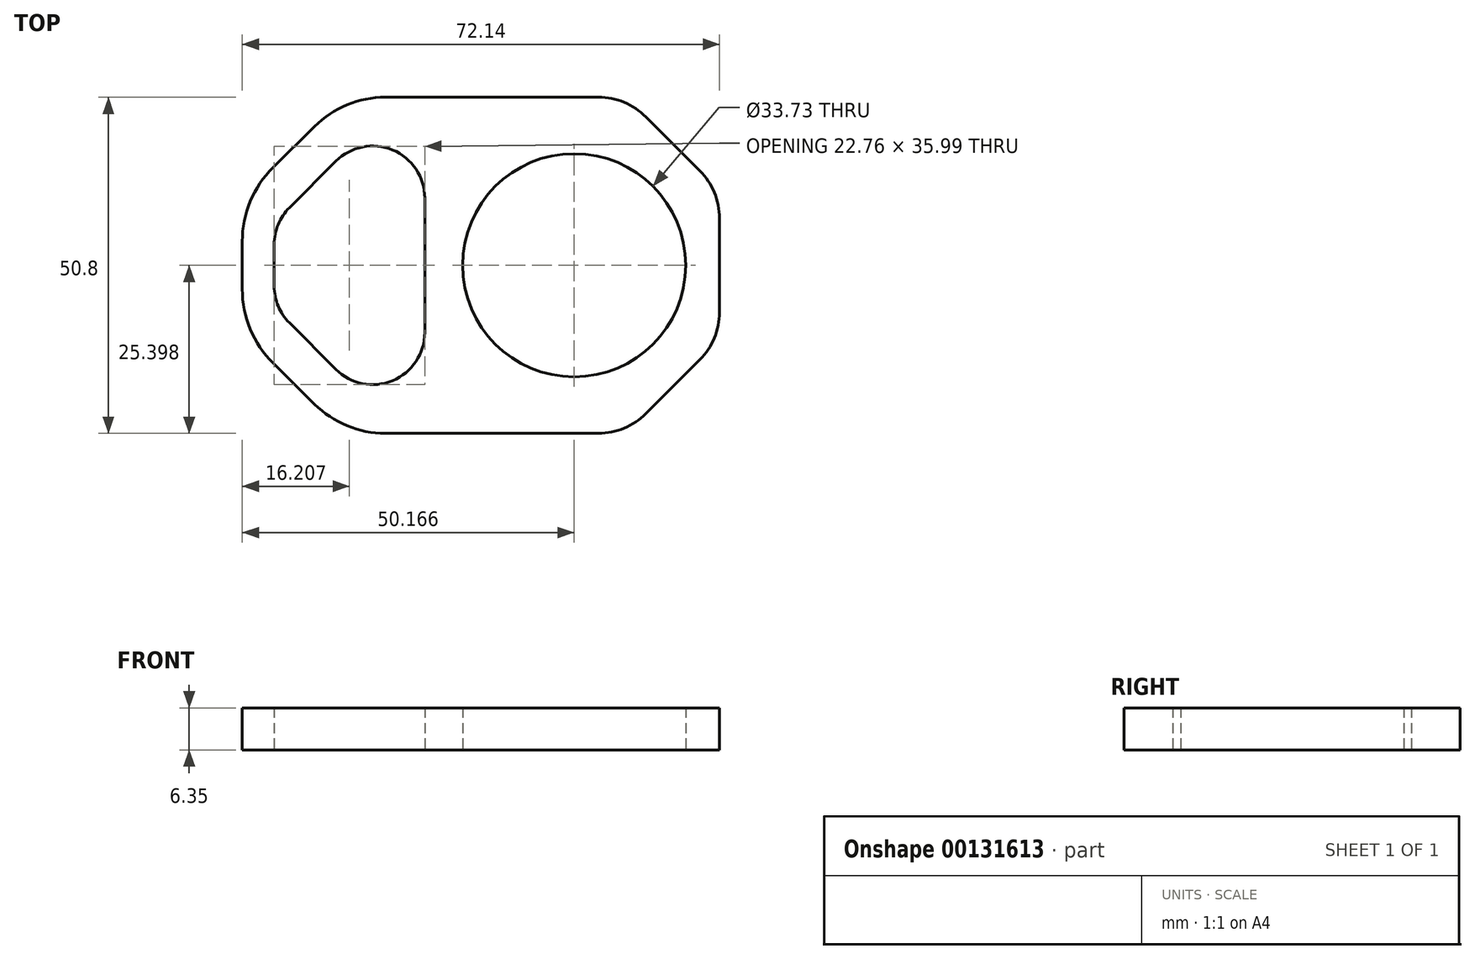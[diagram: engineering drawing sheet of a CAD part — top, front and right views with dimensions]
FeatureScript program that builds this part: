
annotation { "Feature Type Name" : "Feature", "Feature Type Description" : "" }
export const myFeature = defineFeature(function(context is Context, id is Id, definition is map)
    precondition{}
    {
        {
            var Q0;
            Q0=qCreatedBy(makeId("Top.planeOp"),FACE);
            var sketch = newSketch(context, id + "F0", { "sketchPlane" : qUnion([Q0])});
            skCircle(sketch, "E0", {"center": v(50.44, -25.61) * mm, "radius": 16.87 * mm});
            skPoint(sketch, "E1", {"position": v(72.4, -36.91) * mm});
            skPoint(sketch, "E2", {"position": v(58.31, -51.01) * mm});
            skPoint(sketch, "E3.orphan", {"position": v(72.4, -51.01) * mm});
            skLineSegment(sketch, "E4.bottom", {"start": v(72.4, -32.7) * mm, "end": v(72.4, -18.52) * mm});
            skLineSegment(sketch, "E4.top", {"start": v(0.27, -29.21) * mm, "end": v(0.27, -22.01) * mm});
            skLineSegment(sketch, "E4.left", {"start": v(54.1, -51.01) * mm, "end": v(21.91, -51.01) * mm});
            skLineSegment(sketch, "E4.right", {"start": v(54.1, -0.21) * mm, "end": v(21.91, -0.21) * mm});
            skLineSegment(sketch, "E5", {"start": v(61.29, -48.04) * mm, "end": v(69.43, -39.9) * mm});
            skArc(sketch, "E6.filletArc", {"start": v(54.1, -51.01) * mm, "mid": v(58, -50.24) * mm, "end": v(61.29, -48.04) * mm});
            skArc(sketch, "E7.filletArc", {"start": v(69.43, -39.9) * mm, "mid": v(71.63, -36.6) * mm, "end": v(72.4, -32.7) * mm});
            skArc(sketch, "E8.MirrorCS", {"start": v(54.1, -0.21) * mm, "mid": v(58, -0.98) * mm, "end": v(61.29, -3.19) * mm});
            skLineSegment(sketch, "E9.MirrorCS", {"start": v(61.29, -3.19) * mm, "end": v(69.43, -11.33) * mm});
            skArc(sketch, "E10.MirrorCS", {"start": v(69.43, -11.33) * mm, "mid": v(71.63, -14.63) * mm, "end": v(72.4, -18.52) * mm});
            skPoint(sketch, "E11", {"position": v(15.64, -51.01) * mm});
            skPoint(sketch, "E12.MirrorP", {"position": v(15.64, -0.21) * mm});
            skPoint(sketch, "E13", {"position": v(0.27, -35.77) * mm});
            skLineSegment(sketch, "E14", {"start": v(11.18, -46.6) * mm, "end": v(4.93, -40.4) * mm});
            skArc(sketch, "E15.filletArc", {"start": v(11.18, -46.6) * mm, "mid": v(16.11, -49.86) * mm, "end": v(21.91, -51.01) * mm});
            skArc(sketch, "E16.filletArc", {"start": v(0.27, -29.21) * mm, "mid": v(1.48, -35.27) * mm, "end": v(4.93, -40.4) * mm});
            skArc(sketch, "E17.MirrorCS", {"start": v(11.18, -4.63) * mm, "mid": v(16.11, -1.36) * mm, "end": v(21.91, -0.21) * mm});
            skLineSegment(sketch, "E18.MirrorCS", {"start": v(11.18, -4.63) * mm, "end": v(4.93, -10.83) * mm});
            skArc(sketch, "E19.MirrorCS", {"start": v(0.27, -22.01) * mm, "mid": v(1.48, -15.96) * mm, "end": v(4.93, -10.83) * mm});
            skLineSegment(sketch, "E20", {"start": v(19.98, -35.77) * mm, "end": v(27.86, -35.77) * mm});
            skLineSegment(sketch, "E21", {"start": v(27.86, -35.77) * mm, "end": v(27.86, -15.45) * mm});
            skLineSegment(sketch, "E22", {"start": v(5.1, -28.76) * mm, "end": v(5.1, -22.46) * mm});
            skLineSegment(sketch, "E23", {"start": v(19.98, -35.77) * mm, "end": v(19.98, -43.65) * mm});
            skLineSegment(sketch, "E24", {"start": v(14.41, -41.34) * mm, "end": v(7.4, -34.33) * mm});
            skLineSegment(sketch, "E25.MirrorCS", {"start": v(14.41, -9.88) * mm, "end": v(7.4, -16.9) * mm});
            skArc(sketch, "E26.trimOffspring", {"start": v(14.41, -41.34) * mm, "mid": v(23, -43.05) * mm, "end": v(27.86, -35.77) * mm});
            skArc(sketch, "E27.trimOffspring", {"start": v(5.1, -22.46) * mm, "mid": v(5.7, -19.45) * mm, "end": v(7.4, -16.9) * mm});
            skArc(sketch, "E28.trimOffspring", {"start": v(5.1, -28.76) * mm, "mid": v(5.7, -31.77) * mm, "end": v(7.4, -34.33) * mm});
            skArc(sketch, "E29.trimOffspring", {"start": v(14.41, -9.88) * mm, "mid": v(23, -8.18) * mm, "end": v(27.86, -15.45) * mm});
            skPoint(sketch, "E30.trimOffspring.end.orphan", {"position": v(74.5, -25.61) * mm});
            skPoint(sketch, "E31.start.orphan", {"position": v(-2.05, -25.61) * mm});
            skSolve(sketch);
        }
        {
            var Q0;
            Q0=makeQuery(id+"F0.imprint","IMPRINT",FACE,{"disambiguationData":[TD([[makeQuery(id+"F0.imprint","IMPRINT",EDGE,{"derivedFrom":sQuery(id+"F0.wireOp",EDGE,"E0")}),-1.0]])]});
            extrude(context, id + "F1", {"entities" : qUnion([Q0]), "depth" : 6.35 * mm});
        }
    });
